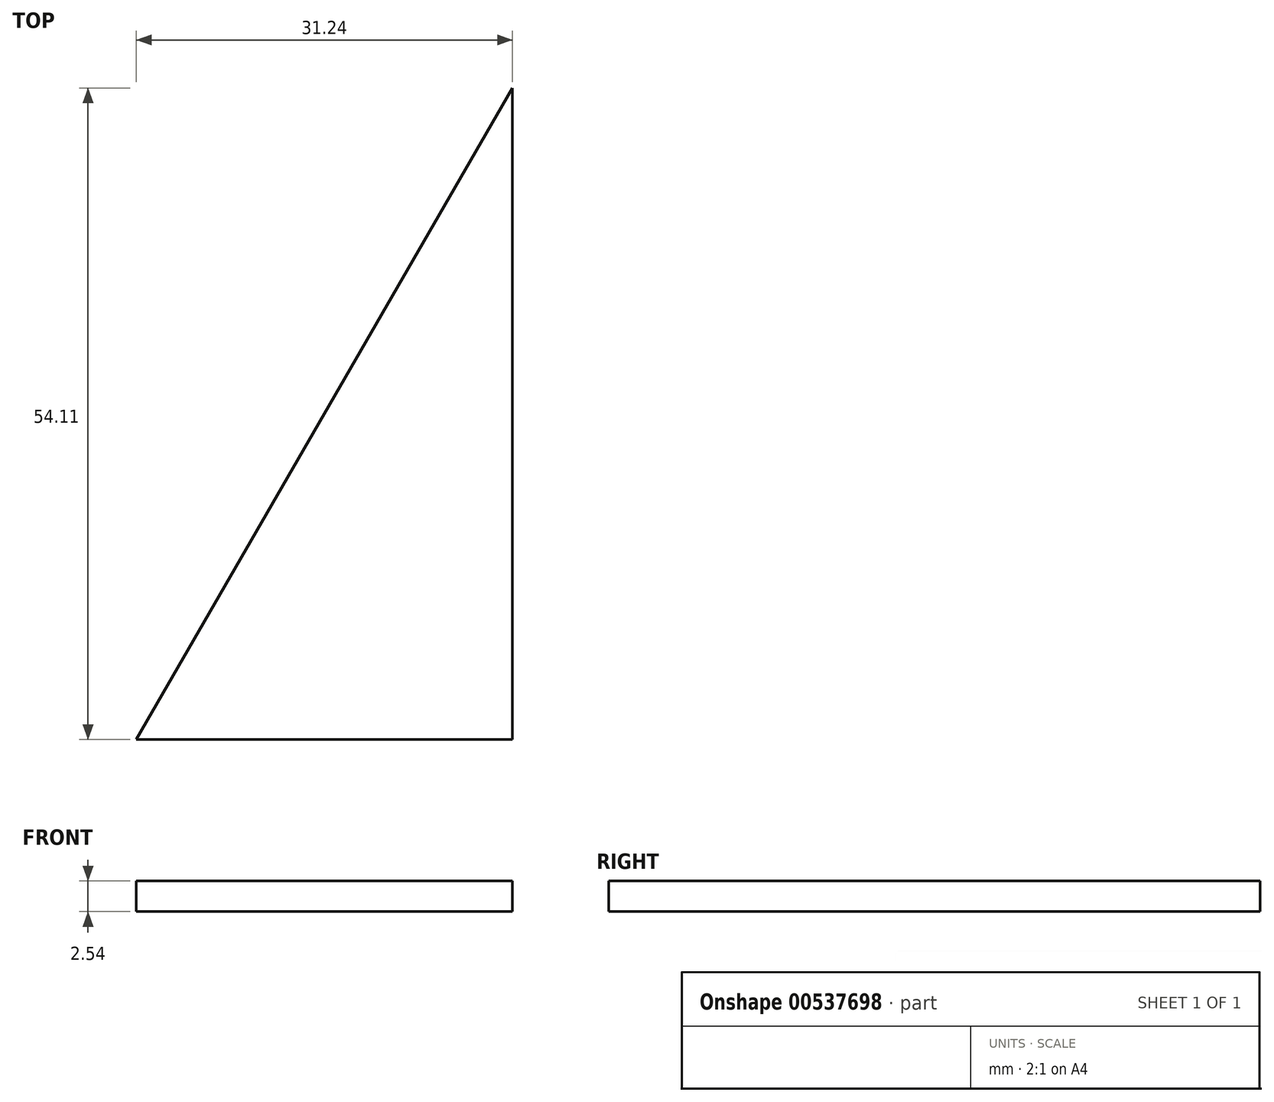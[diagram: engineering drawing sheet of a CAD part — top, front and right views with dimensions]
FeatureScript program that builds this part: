
annotation { "Feature Type Name" : "Feature", "Feature Type Description" : "" }
export const myFeature = defineFeature(function(context is Context, id is Id, definition is map)
    precondition{}
    {
        {
            var Q0;
            Q0=qCreatedBy(makeId("Top.planeOp"),FACE);
            var sketch = newSketch(context, id + "F0", { "sketchPlane" : qUnion([Q0])});
            skLineSegment(sketch, "E0", {"start": v(0, 54.1) * mm, "end": v(-31.24, 0) * mm});
            skLineSegment(sketch, "E1", {"start": v(-31.24, 0) * mm, "end": v(0, 0) * mm});
            skLineSegment(sketch, "E2", {"start": v(0, 0) * mm, "end": v(0, 54.1) * mm});
            skSolve(sketch);
        }
        {
            var Q0;
            Q0=makeQuery(id+"F0.imprint","IMPRINT",FACE,{"disambiguationData":[TD([[makeQuery(id+"F0.imprint","IMPRINT",EDGE,{"derivedFrom":sQuery(id+"F0.wireOp",EDGE,"E0")}),1.0]])]});
            extrude(context, id + "F1", {"entities" : qUnion([Q0]), "depth" : 2.54 * mm, "offsetDistance" : 25.4 * mm});
        }
    });
